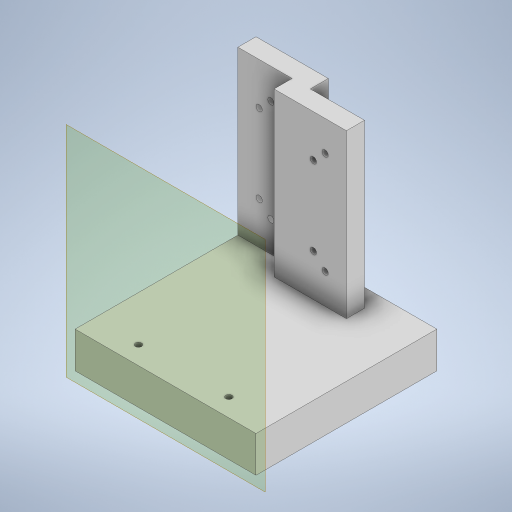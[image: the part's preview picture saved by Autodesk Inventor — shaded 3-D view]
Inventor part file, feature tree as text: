
AUTODESK INVENTOR PART (.ipt)
format: ipt  version: 2023 (Build 270158000, 158)  size: 349,696 bytes
history: native  units: mm
features: sketch x7, extrude x4, hole x3, other x1, mirror x1, plane x1, split x1
ambient origin geometry x8: Origin, YZ Plane, XZ Plane, XY Plane, X Axis, Y Axis, Z Axis, Center Point
bodies: Body1 (feature_tree)
feature tree (18):
  other  "Sólido1"
  extrude  "Extrusión1"  Depth=90.0mm
  hole  "Agujero1"  [1 undecoded]
  extrude  "Extrusión2"  TaperAngle=0.0deg  [1 undecoded]
  extrude  "Extrusión3"  Depth=90.0mm
  hole  "Agujero2"  [1 undecoded]
  extrude  "Extrusión4"  Depth=10.0mm TaperAngle=0.0deg
  mirror  "Simetría1"
  plane  "Plano de trabajo2"
  hole  "Agujero3"  [1 undecoded]
  split  "Dividir1"
  sketch  "Boceto1"  dims[d0=30.0mm d1=90.0mm]
  sketch  "Boceto2"  dims[d2=10.0mm d3=0.0mm]
  sketch  "Boceto3"  dims[d4=1.75mm d5=1.75mm d6=1.75mm d7=1.75mm d8=10.0mm d9=10.0mm d10=10.0mm d11=15.0mm d12=0.0mm]
  sketch  "Boceto4"  dims[d13=30.0mm d14=0.0mm]
  sketch  "Boceto5"  dims[d15=90.0mm d16=15.0mm]
  sketch  "Boceto6"  dims[d17=3.5mm d18=6.0mm d19=4.0mm d20=2.0mm d21=90.0deg d22=8.0mm d23=20.594885mm d24=20.0mm]
  sketch  "Boceto7"  dims[d25=90.0mm d26=10.0mm d27=0.0mm d28=30.0mm d29=0.0mm d30=3.5mm d31=1.75mm d32=1.75mm d33=1.75mm d34=1.75mm d35=10.0mm d36=10.0mm d38=10.0mm d39=-41.10961mm d40=15.0mm d41=0.0mm d42=15.0mm d43=90.0mm d45=0.0mm d46=3.5mm d47=6.0mm d48=4.0mm d49=2.0mm d50=90.0deg d51=8.0mm d52=20.594885mm d53=20.0mm d54=100.0mm d55=0.0mm d56=5.0mm d57=5.0mm d58=3.5mm d59=5.0mm d60=5.0mm d61=10.0mm d62=30.0mm d64=20.0mm d65=3.5mm d66=6.0mm d67=4.0mm d68=2.0mm d69=90.0deg d70=8.0mm d71=20.594885mm]
note: 4 required parameter values undecoded (feature->parameter linkage not recoverable at this tier; creation-order binding heuristic only, values carry confidence <= 0.55)
